# Revit family: HVAC_Ductwork_Airzone_Motorized-Plenum_Mitsubishi-Electric_Low-Profile_4-Dampers
name_source: partatom
category: Mechanical Equipment
revit_build: Autodesk Revit 2016 (Build: 20150714_1515(x64)
units: mm (PartAtom-declared; Revit-internal decimal feet)

## family parameters
Always vertical = Yes
Cut with Voids When Loaded = No
OmniClass Number = 23.75.70.14
OmniClass Title = Air Ductwork
Part Type = Normal
Room Calculation Point = No
Round Connector Dimension = Use Diameter
Shared = No
Work Plane-Based = No

## types (1)
- MELSL01M4
    Apparent Load = 58 VA
    Dampers Diameter = 150.000 mm
    Dampers Length = 149.000 mm
    Description = Airzone low profile motorized plenum with neck that mechanically adapts to the main ducted AC units of Mitsubishi Electric.
    Disclaimer = All information provided in this model is reviewed before being published. However, Airzone cannot guarantee this model is error-free, therefore users are strongly encouraged to check for technical documentation and updates
    Fresh Air Inlet Connection Height = 75.000 mm
    Fresh Air Inlet Connection Offset Height = 48.305 mm
    Fresh Air Inlet Connection Width = 175.000 mm
    Insulated Body Height = 210.000 mm
    Insulated Body Length = 930.000 mm
    Insulated Body Material = Metal -AIRZONE - Insulating Lining -Aluminum Finish
    Insulated Body Width = 255.000 mm
    Load Classification = Other
    Main Control Board Depth = 57.000 mm
    Main Control Board Height = 180.000 mm
    Main Control Board Material = Plastic - AIRZONE - Smooth - Off-white
    Main Control Board Width = 195.000 mm
    Manufacturer = AIRZONE
    Material = Metal - AIRZONE - Galvanized Sheet - Semi-polished
    Model = MEISL01M4
    Neck Bottom Offset = 30.200 mm
    Neck Height = 153.600 mm
    Neck Length = 40.000 mm
    Neck Side Offset = 33.200 mm
    Neck Width = 863.600 mm
    Power Factor = 1
    Product Comments = Refer to technical documentation for further details
    Product Documentation Download URL = http://doc.airzone.es
    Revit Model Version = 1.0
    Type Image = <None>
    Type Image Comments = Image available in product documentation download
    URL = www.airzone.es
    Voltage = 230 V

## geometry (parser evidence)
native form markers: Extrusion x2, Sweep x3
no freeform markers — native parametric forms only
